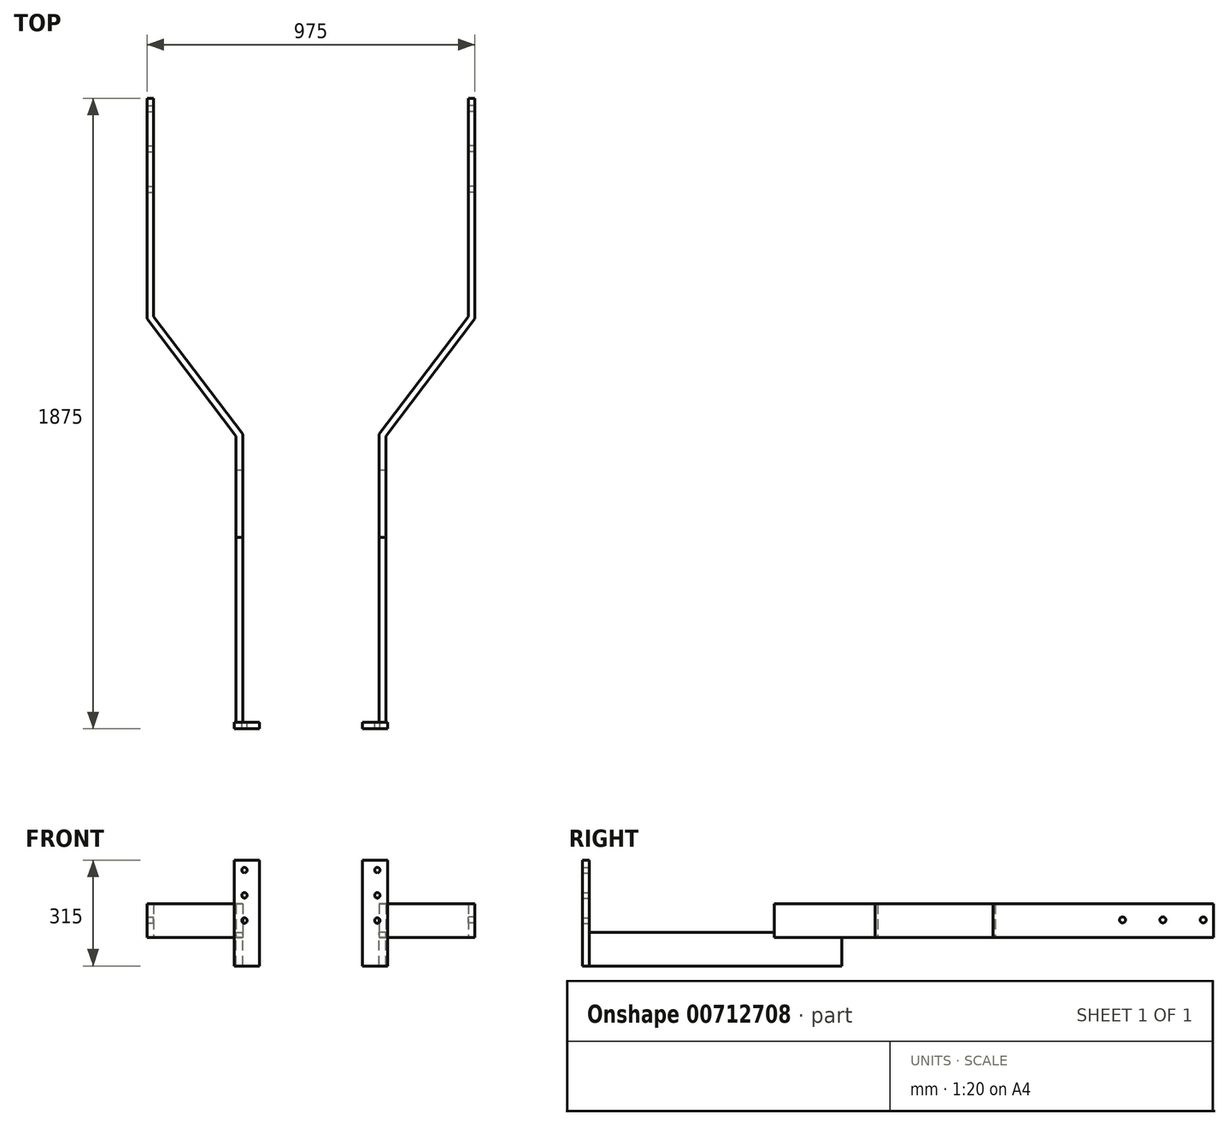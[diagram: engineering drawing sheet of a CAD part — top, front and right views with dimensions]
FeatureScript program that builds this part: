
annotation { "Feature Type Name" : "Feature", "Feature Type Description" : "" }
export const myFeature = defineFeature(function(context is Context, id is Id, definition is map)
    precondition{}
    {
        {
            var Q0;
            Q0=qCreatedBy(makeId("Top.planeOp"),FACE);
            var sketch = newSketch(context, id + "F0", { "sketchPlane" : qUnion([Q0])});
            skLineSegment(sketch, "E0", {"start": v(-202.5, 0) * mm, "end": v(-202.5, 750) * mm});
            skLineSegment(sketch, "E1", {"start": v(-202.5, 750) * mm, "end": v(-222.5, 750) * mm});
            skLineSegment(sketch, "E2", {"start": v(-222.5, 750) * mm, "end": v(-222.5, 0) * mm});
            skLineSegment(sketch, "E3", {"start": v(-222.5, 0) * mm, "end": v(-202.5, 0) * mm});
            skSolve(sketch);
        }
        {
            var Q0;
            Q0=makeQuery(id+"F0.imprint","IMPRINT",FACE,{"disambiguationData":[TD([[makeQuery(id+"F0.imprint","IMPRINT",EDGE,{"derivedFrom":sQuery(id+"F0.wireOp",EDGE,"E0")}),1.0]])]});
            extrude(context, id + "F1", {"entities" : qUnion([Q0]), "oppositeDirection" : true, "depth" : 100 * mm, "offsetDistance" : 25 * mm});
        }
        {
            var Q0;
            Q0=makeQuery(id+"F1.opExtrude","SWEPT_FACE",FACE,{"disambiguationData":[OSD([sQuery(id+"F0.wireOp",EDGE,"E0")])]});
            var sketch = newSketch(context, id + "F2", { "sketchPlane" : qUnion([Q0])});
            skLineSegment(sketch, "E4", {"start": v(550, 0) * mm, "end": v(550, -15) * mm});
            skLineSegment(sketch, "E5", {"start": v(550, -15) * mm, "end": v(750, -15) * mm});
            skSolve(sketch);
        }
        {
            var Q0;
            {var subQ0=sQuery(id+"F2.wireOp",EDGE,"E4");Q0=makeQuery(id+"F2.imprint","IMPRINT",FACE,{"disambiguationData":[TD([[makeQuery(id+"F2.imprint","IMPRINT",EDGE,{"derivedFrom":subQ0}),1.0]])]});}
            extrude(context, id + "F3", {"entities" : qUnion([Q0]), "operationType" : NewBodyOperationType.REMOVE, "endBound" : BoundingType.THROUGH_ALL, "oppositeDirection" : true, "depth" : 25 * mm, "offsetDistance" : 25 * mm});
        }
        {
            var Q0;
            Q0=makeQuery(id+"F3.boolean.opBoolean","COPY",FACE,{"derivedFrom":makeQuery(id+"F3.opExtrude","SWEPT_FACE",FACE,{"disambiguationData":[OSD([sQuery(id+"F2.wireOp",EDGE,"E5")])]})});
            var sketch = newSketch(context, id + "F4", { "sketchPlane" : qUnion([Q0])});
            skLineSegment(sketch, "E6", {"start": v(-222.5, 550) * mm, "end": v(-222.5, 850) * mm});
            skLineSegment(sketch, "E7", {"start": v(-222.5, 850) * mm, "end": v(-487.5, 1200) * mm});
            skLineSegment(sketch, "E8", {"start": v(-487.5, 1200) * mm, "end": v(-487.5, 1855) * mm});
            skLineSegment(sketch, "E9.0", {"start": v(-467.5, 1206.72) * mm, "end": v(-467.5, 1855) * mm});
            skLineSegment(sketch, "E9.1", {"start": v(-202.5, 856.72) * mm, "end": v(-467.5, 1206.72) * mm});
            skLineSegment(sketch, "E9.2", {"start": v(-202.5, 550) * mm, "end": v(-202.5, 856.72) * mm});
            skLineSegment(sketch, "E10", {"start": v(-487.5, 1855) * mm, "end": v(-467.5, 1855) * mm});
            skSolve(sketch);
        }
        {
            var Q0;
            {var subQ0=sQuery(id+"F4.wireOp",EDGE,"E7");Q0=makeQuery(id+"F4.imprint","IMPRINT",FACE,{"disambiguationData":[TD([[makeQuery(id+"F4.imprint","IMPRINT",EDGE,{"derivedFrom":subQ0}),-1.0]])]});}
            var Q1;
            {var subQ1=sQuery(id+"F2.wireOp",EDGE,"E5");var subQ3=makeQuery(id+"F3.boolean.opBoolean","COPY",EDGE,{"derivedFrom":makeQuery(id+"F3.opExtrude","SWEPT_EDGE",EDGE,{"disambiguationData":[OSD([sQuery(id+"F2.wireOp",EDGE,"E4"),subQ1])]})});Q1=makeQuery(id+"F4.imprint","IMPRINT",FACE,{"disambiguationData":[TD([[makeQuery(id+"F4.imprint","IMPRINT",EDGE,{"derivedFrom":subQ3}),1.0]])]});}
            extrude(context, id + "F5", {"entities" : qUnion([Q0, Q1]), "depth" : 100 * mm, "offsetDistance" : 25 * mm});
        }
        {
            var Q0;
            Q0=makeQuery(id+"F5.opExtrude","SWEPT_FACE",FACE,{"disambiguationData":[OSD([sQuery(id+"F4.wireOp",EDGE,"E9.0")])]});
            var sketch = newSketch(context, id + "F6", { "sketchPlane" : qUnion([Q0])});
            skCircle(sketch, "E11", {"center": v(1825, 37) * mm, "radius": 9 * mm});
            skCircle(sketch, "E12", {"center": v(1705, 37) * mm, "radius": 9 * mm});
            skCircle(sketch, "E13", {"center": v(1585, 37) * mm, "radius": 9 * mm});
            skSolve(sketch);
        }
        {
            var Q0;
            Q0=makeQuery(id+"F6.imprint","IMPRINT",FACE,{"disambiguationData":[TD([[makeQuery(id+"F6.imprint","IMPRINT",EDGE,{"derivedFrom":sQuery(id+"F6.wireOp",EDGE,"E13")}),1.0]])]});
            var Q1;
            Q1=makeQuery(id+"F6.imprint","IMPRINT",FACE,{"disambiguationData":[TD([[makeQuery(id+"F6.imprint","IMPRINT",EDGE,{"derivedFrom":sQuery(id+"F6.wireOp",EDGE,"E12")}),1.0]])]});
            var Q2;
            Q2=makeQuery(id+"F6.imprint","IMPRINT",FACE,{"disambiguationData":[TD([[makeQuery(id+"F6.imprint","IMPRINT",EDGE,{"derivedFrom":sQuery(id+"F6.wireOp",EDGE,"E11")}),1.0]])]});
            extrude(context, id + "F7", {"entities" : qUnion([Q0, Q1, Q2]), "operationType" : NewBodyOperationType.REMOVE, "endBound" : BoundingType.THROUGH_ALL, "oppositeDirection" : true, "depth" : 25 * mm, "offsetDistance" : 25 * mm});
        }
        {
            var Q0;
            Q0=makeQuery(id+"F1.opExtrude","SWEPT_FACE",FACE,{"disambiguationData":[OSD([sQuery(id+"F0.wireOp",EDGE,"E3")])]});
            var sketch = newSketch(context, id + "F8", { "sketchPlane" : qUnion([Q0])});
            skLineSegment(sketch, "E14", {"start": v(-227.5, -100) * mm, "end": v(-227.5, 215) * mm});
            skLineSegment(sketch, "E15", {"start": v(-227.5, 215) * mm, "end": v(-152.5, 215) * mm});
            skLineSegment(sketch, "E16", {"start": v(-152.5, 215) * mm, "end": v(-152.5, -100) * mm});
            skLineSegment(sketch, "E17", {"start": v(-227.5, -100) * mm, "end": v(-152.5, -100) * mm});
            skCircle(sketch, "E18", {"center": v(-197.5, 185) * mm, "radius": 8 * mm});
            skCircle(sketch, "E19", {"center": v(-197.5, 110) * mm, "radius": 8 * mm});
            skCircle(sketch, "E20", {"center": v(-197.5, 35) * mm, "radius": 8 * mm});
            skSolve(sketch);
        }
        {
            var Q0;
            {var subQ5=sQuery(id+"F8.wireOp",EDGE,"E14");Q0=makeQuery(id+"F8.imprint","IMPRINT",FACE,{"disambiguationData":[TD([[makeQuery(id+"F8.imprint","IMPRINT",EDGE,{"derivedFrom":subQ5}),-1.0]])]});}
            var Q1;
            {var subQ1=sQuery(id+"F0.wireOp",EDGE,"E3");Q1=makeQuery(id+"F8.imprint","IMPRINT",FACE,{"disambiguationData":[TD([[makeQuery(id+"F8.imprint","IMPRINT",EDGE,{"derivedFrom":makeQuery(id+"F1.opExtrude","CAP_EDGE",EDGE,{"disambiguationData":[OSD([subQ1])],"isStart":true})}),-1.0]])]});}
            extrude(context, id + "F9", {"entities" : qUnion([Q0, Q1]), "depth" : 20 * mm, "offsetDistance" : 25 * mm});
        }
        {
            var Q0;
            Q0=makeQuery(id+"F5.opExtrude","SWEPT_BODY",BODY,{"disambiguationData":[OSD([sQuery(id+"F2.wireOp",EDGE,"E4"),sQuery(id+"F2.wireOp",EDGE,"E5"),sQuery(id+"F4.wireOp",EDGE,"E6"),sQuery(id+"F4.wireOp",EDGE,"E7"),sQuery(id+"F4.wireOp",EDGE,"E8"),sQuery(id+"F4.wireOp",EDGE,"E9.0"),sQuery(id+"F4.wireOp",EDGE,"E9.1"),sQuery(id+"F4.wireOp",EDGE,"E9.2"),sQuery(id+"F4.wireOp",EDGE,"E10")])]});
            var Q1;
            Q1=makeQuery(id+"F1.opExtrude","SWEPT_BODY",BODY,{"disambiguationData":[OSD([sQuery(id+"F0.wireOp",EDGE,"E0"),sQuery(id+"F0.wireOp",EDGE,"E1"),sQuery(id+"F0.wireOp",EDGE,"E2"),sQuery(id+"F0.wireOp",EDGE,"E3")])]});
            var Q2;
            Q2=makeQuery(id+"F9.opExtrude","SWEPT_BODY",BODY,{"disambiguationData":[OSD([sQuery(id+"F8.wireOp",EDGE,"E14"),sQuery(id+"F8.wireOp",EDGE,"E15"),sQuery(id+"F8.wireOp",EDGE,"E16"),sQuery(id+"F8.wireOp",EDGE,"E17"),sQuery(id+"F8.wireOp",EDGE,"E18"),sQuery(id+"F8.wireOp",EDGE,"E19"),sQuery(id+"F8.wireOp",EDGE,"E20")])]});
            var Q3;
            Q3=qCreatedBy(makeId("Right.planeOp"),FACE);
            mirror(context, id + "F10", {"entities" : qUnion([Q0, Q1, Q2]), "mirrorPlane" : qUnion([Q3])});
        }
    });
